# Revit family: Interceptor-Grease_Low-Profile-Zurn-GT2701
name_source: partatom
category: Plumbing Fixtures
units: mm (PartAtom-declared; Revit-internal decimal feet)

## family parameters
Always vertical = Yes
Cut with Voids When Loaded = No
Maintain Annotation Orientation = No
OmniClass Number = 23.45.30.00
OmniClass Title = Washing and Waste Disposal Equipment
Part Type = Normal
Room Calculation Point = No
Round Connector Dimension = Use Radius
Shared = No
Work Plane-Based = No

## types (3) — shared parameters
Assembly Code = D2090300
CW Connection = No
Default Elevation = 17 "
Description = LOW PROFILE GREASE INTERCEPTOR
HW Connection = No
Main Material = Fabricated Steel - Zurn- Acid resistant Coated
Manufacturer = Zurn Water, LLC
Manufacurer Brand = Zurn
Modified Date = 09/04/25
Product Documentation Link = https://files.zurn.com
Product Page URL = https://www.zurn.com
Product data url = https://www.bimobject.com
URL = www.zurn.com
Vent Connection = No
WFU = 1
Waste Connection = Yes
zero-valued in all types: CWFU, HWFU

## per-type parameters (varying)
| type | Approx. Weight (Lbs) | C | Connector Radius | D/E | F | G | Model | Pipe Size "A" (Inner) | Pipe Size "A" (Nominal) | Pipe Size "A" (outer) |
| GT2701-20 (3 Inch 20 GPM) | 102 " | 10 " | 1.5 " | 3.125 " | 32.375 " | 20.75 " | GT2701-20 | 3.068 " | 3 " | 3.5 " |
| GT2701-35 (4 Inch 35 GPM) | 172 " | 10.75 " | 2 " | 3.313 " | 43.5 " | 29 " | GT2701-35 | 4.026 " | 4 " | 4.5 " |
| GT2701-50 (4 Inch 50 GPM) | 210 " | 16 " | 2 " | 10 " | 49.875 " | 29 " | GT2701-50 | 4.026 " | 4 " | 4.5 " |

## geometry (parser evidence)
native form markers: Sweep x2
no freeform markers — native parametric forms only
